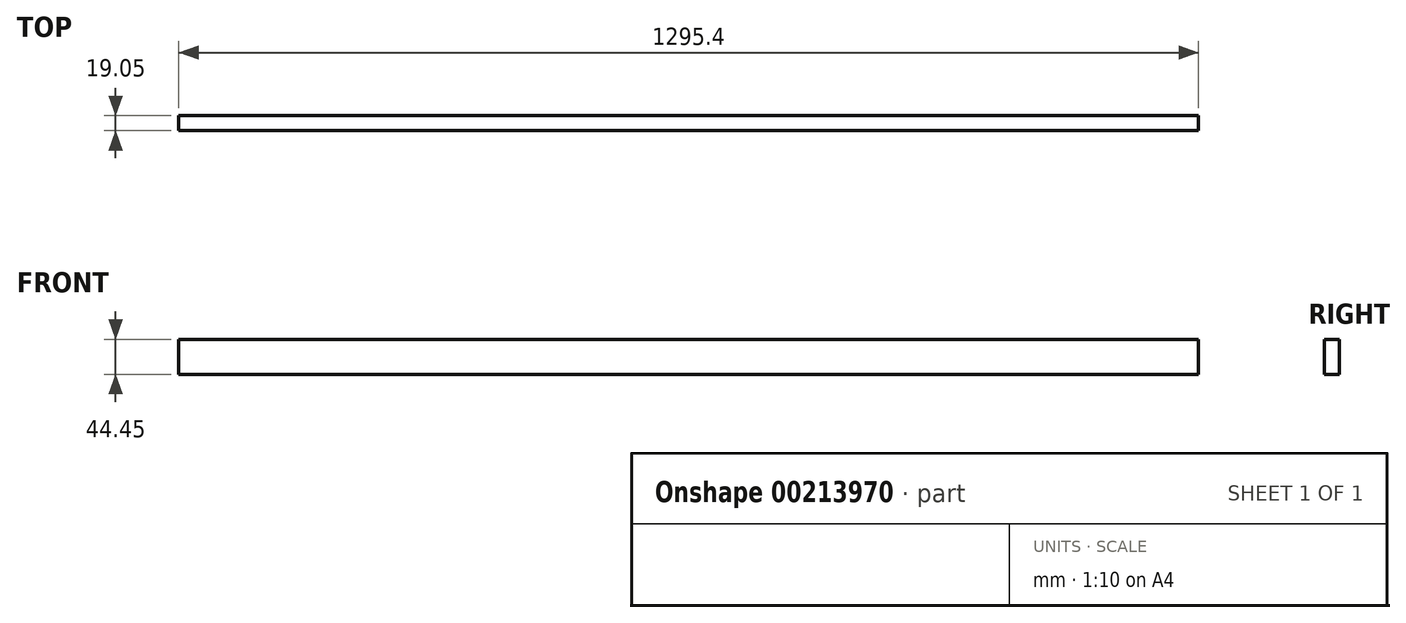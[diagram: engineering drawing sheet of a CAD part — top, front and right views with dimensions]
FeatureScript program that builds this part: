
annotation { "Feature Type Name" : "Feature", "Feature Type Description" : "" }
export const myFeature = defineFeature(function(context is Context, id is Id, definition is map)
    precondition{}
    {
        {
            var Q0;
            Q0=qCreatedBy(makeId("Front.planeOp"),FACE);
            var sketch = newSketch(context, id + "F0", { "sketchPlane" : qUnion([Q0])});
            skLineSegment(sketch, "E0.bottom", {"start": v(-647.7, 0) * mm, "end": v(647.7, 0) * mm});
            skLineSegment(sketch, "E0.top", {"start": v(-647.7, 44.45) * mm, "end": v(647.7, 44.45) * mm});
            skLineSegment(sketch, "E0.left", {"start": v(-647.7, 0) * mm, "end": v(-647.7, 44.45) * mm});
            skLineSegment(sketch, "E0.right", {"start": v(647.7, 0) * mm, "end": v(647.7, 44.45) * mm});
            skSolve(sketch);
        }
        {
            var Q0;
            Q0 = qSketchRegion(id + "F0", true);
            extrude(context, id + "F1", {"entities" : qUnion([Q0]), "depth" : 19.05 * mm});
        }
    });
